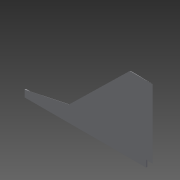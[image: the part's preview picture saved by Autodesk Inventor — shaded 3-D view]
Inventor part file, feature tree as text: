
AUTODESK INVENTOR PART (.ipt)
format: ipt  version: 2014 SP1 (Build 180222100, 222)  size: 187,392 bytes
history: native  units: mm
features: sketch x4, plane x3, loft x2, extrude x1, other x1, projected_geometry x1
ambient origin geometry x8: Origin, YZ Plane, XZ Plane, XY Plane, X Axis, Y Axis, Z Axis, Center Point
bodies: Solid1 (feature_tree)
feature tree (12):
  sketch  "Sketch1"  dims[d2=35.0mm d4=220.0mm]
  plane  "Work Plane1"
  sketch  "Sketch2"  dims[d5=85.0mm d6=0.0mm d7=90.0deg]
  plane  "Work Plane2"
  loft  "Loft1"
  loft  "Loft2"
  plane  "Work Plane3"
  extrude  "Extrusion1"  TaperAngle=0.0deg  [1 undecoded]
  sketch  "Sketch3"  dims[d8=0.0mm d9=90.0deg d10=0.0mm d11=90.0deg]
  other  "Edges1"
  sketch  "Sketch4"  dims[d12=0.0mm d13=90.0deg d14=0.0mm d16=450.0mm d17=5.0mm d18=450.0mm d19=25.0mm d20=0.0mm]
  projected_geometry  "Projected Loop1"
note: 1 required parameter value undecoded (feature->parameter linkage not recoverable at this tier; creation-order binding heuristic only, values carry confidence <= 0.55)
